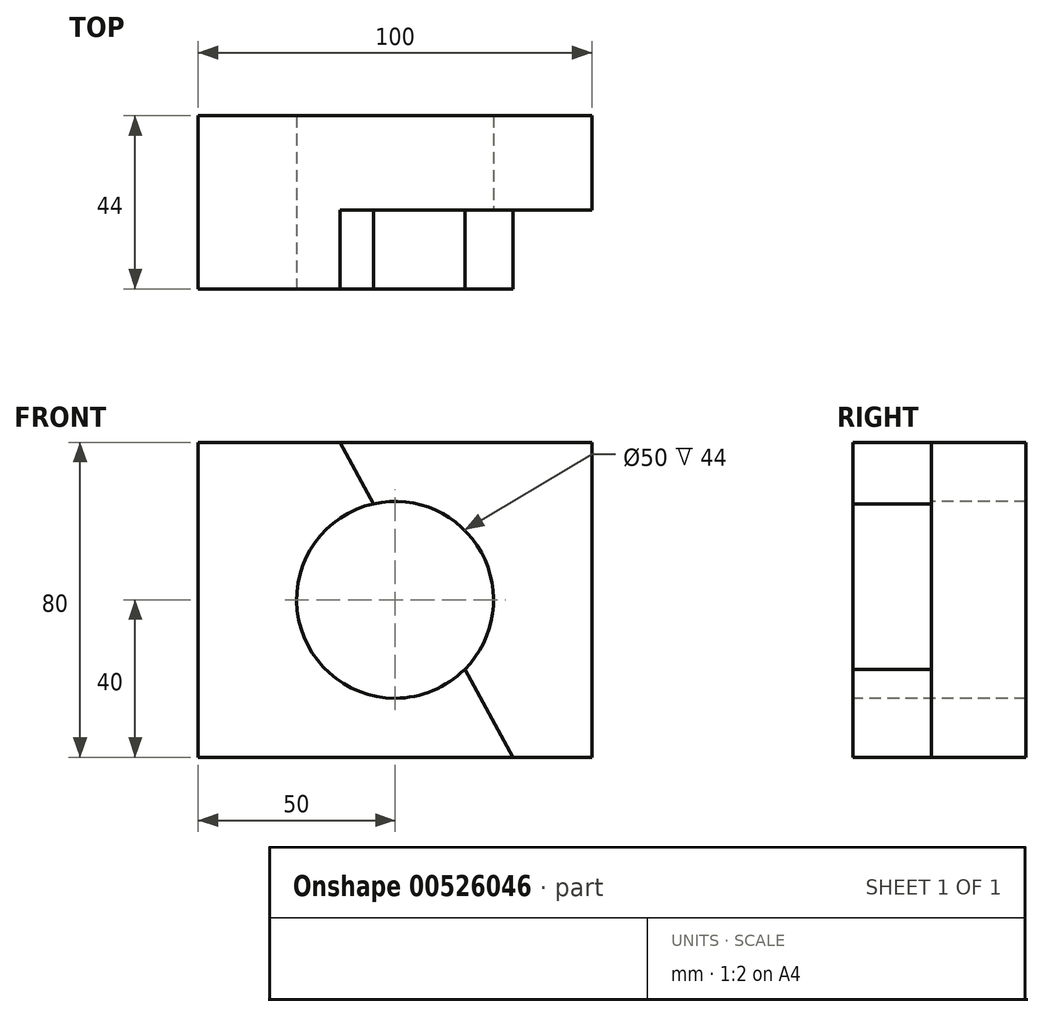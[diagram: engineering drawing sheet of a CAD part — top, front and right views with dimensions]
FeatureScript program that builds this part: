
annotation { "Feature Type Name" : "Feature", "Feature Type Description" : "" }
export const myFeature = defineFeature(function(context is Context, id is Id, definition is map)
    precondition{}
    {
        {
            var Q0;
            Q0=qCreatedBy(makeId("Front.planeOp"),FACE);
            var sketch = newSketch(context, id + "F0", { "sketchPlane" : qUnion([Q0])});
            skLineSegment(sketch, "E0.bottom", {"start": v(50, 40) * mm, "end": v(-50, 40) * mm});
            skLineSegment(sketch, "E0.top", {"start": v(50, -40) * mm, "end": v(-50, -40) * mm});
            skLineSegment(sketch, "E0.left", {"start": v(50, 40) * mm, "end": v(50, -40) * mm});
            skLineSegment(sketch, "E0.right", {"start": v(-50, 40) * mm, "end": v(-50, -40) * mm});
            skPoint(sketch, "E0.middle", {"position": v(0, 0) * mm});
            skSolve(sketch);
        }
        {
            var Q0;
            Q0=makeQuery(id+"F0.imprint","IMPRINT",FACE,{"disambiguationData":[TD([[makeQuery(id+"F0.imprint","IMPRINT",EDGE,{"derivedFrom":sQuery(id+"F0.wireOp",EDGE,"E0.bottom")}),1.0]])]});
            extrude(context, id + "F1", {"entities" : qUnion([Q0]), "endBound" : BoundingType.SYMMETRIC, "depth" : 44 * mm, "offsetDistance" : 25 * mm});
        }
        {
            var Q0;
            Q0=makeQuery(id+"F1.opExtrude","CAP_FACE",FACE,{"disambiguationData":[OSD([sQuery(id+"F0.wireOp",EDGE,"E0.bottom"),sQuery(id+"F0.wireOp",EDGE,"E0.top"),sQuery(id+"F0.wireOp",EDGE,"E0.left"),sQuery(id+"F0.wireOp",EDGE,"E0.right")])],"isStart":false});
            var sketch = newSketch(context, id + "F2", { "sketchPlane" : qUnion([Q0])});
            skLineSegment(sketch, "E1", {"start": v(30, -40) * mm, "end": v(-14, 40) * mm});
            skLineSegment(sketch, "E2", {"start": v(-14, 40) * mm, "end": v(50, 40) * mm});
            skLineSegment(sketch, "E3", {"start": v(50, 40) * mm, "end": v(50, -40) * mm});
            skLineSegment(sketch, "E4", {"start": v(50, -40) * mm, "end": v(30, -40) * mm});
            skSolve(sketch);
        }
        {
            var Q0;
            Q0=makeQuery(id+"F2.imprint","IMPRINT",FACE,{"disambiguationData":[TD([[makeQuery(id+"F2.imprint","IMPRINT",EDGE,{"derivedFrom":sQuery(id+"F2.wireOp",EDGE,"E1")}),-1.0]])]});
            extrude(context, id + "F3", {"entities" : qUnion([Q0]), "operationType" : NewBodyOperationType.REMOVE, "oppositeDirection" : true, "depth" : 20 * mm, "offsetDistance" : 25 * mm});
        }
        {
            var Q0;
            Q0=makeQuery(id+"F1.opExtrude","CAP_FACE",FACE,{"disambiguationData":[OSD([sQuery(id+"F0.wireOp",EDGE,"E0.bottom"),sQuery(id+"F0.wireOp",EDGE,"E0.top"),sQuery(id+"F0.wireOp",EDGE,"E0.left"),sQuery(id+"F0.wireOp",EDGE,"E0.right")])],"isStart":false});
            var sketch = newSketch(context, id + "F4", { "sketchPlane" : qUnion([Q0])});
            skCircle(sketch, "E5", {"center": v(0, 0) * mm, "radius": 25 * mm});
            skSolve(sketch);
        }
        {
            var Q0;
            {var subQ0=sQuery(id+"F4.wireOp",EDGE,"E5");var subQ1=makeQuery(id+"F3.boolean.opBoolean","COPY",EDGE,{"derivedFrom":makeQuery(id+"F3.opExtrude","CAP_EDGE",EDGE,{"disambiguationData":[OSD([sQuery(id+"F2.wireOp",EDGE,"E1")])],"isStart":true})});var subQ2=makeQuery(id+"F4.imprint","INTERSECT",VERTEX,{"disambiguationData":[OD(0.0)],"derivedFrom":[subQ1,subQ0]});Q0=makeQuery(id+"F4.imprint","IMPRINT",FACE,{"disambiguationData":[TD([[makeQuery(id+"F4.imprint","IMPRINT",EDGE,{"disambiguationData":[TD([[subQ2,1.0]])],"derivedFrom":subQ0}),1.0]])]});}
            var Q1;
            {var subQ0=sQuery(id+"F4.wireOp",EDGE,"E5");var subQ1=makeQuery(id+"F3.boolean.opBoolean","COPY",EDGE,{"derivedFrom":makeQuery(id+"F3.opExtrude","CAP_EDGE",EDGE,{"disambiguationData":[OSD([sQuery(id+"F2.wireOp",EDGE,"E1")])],"isStart":true})});var subQ2=makeQuery(id+"F4.imprint","INTERSECT",VERTEX,{"disambiguationData":[OD(0.0)],"derivedFrom":[subQ1,subQ0]});Q1=makeQuery(id+"F4.imprint","IMPRINT",FACE,{"disambiguationData":[TD([[makeQuery(id+"F4.imprint","IMPRINT",EDGE,{"disambiguationData":[TD([[subQ2,-1.0]])],"derivedFrom":subQ0}),1.0]])]});}
            extrude(context, id + "F5", {"entities" : qUnion([Q0, Q1]), "operationType" : NewBodyOperationType.REMOVE, "endBound" : BoundingType.THROUGH_ALL, "oppositeDirection" : true, "depth" : 25 * mm, "offsetDistance" : 25 * mm});
        }
    });
